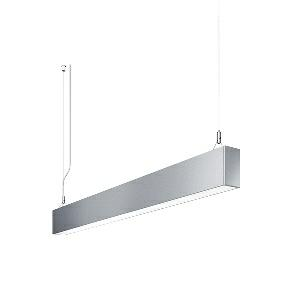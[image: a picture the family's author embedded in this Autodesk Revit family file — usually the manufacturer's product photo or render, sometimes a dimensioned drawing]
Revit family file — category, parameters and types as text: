
# Revit family: idoo_line_-_ilp_4000_vtl_d_00806468_3267
name_source: partatom
category: Lighting Fixtures
units: mm (PartAtom-declared; Revit-internal decimal feet)

## family parameters
Cut with Voids When Loaded = No
Host = Face
Light Source = No
Part Type = Normal
Room Calculation Point = No
Round Connector Dimension = Use Diameter
Shared = No

## types (1)
- IDOO.line - ILP 4000/VTL/D (1 x LED, 3850 lm, 2700-6500K)
    Apparent Load = 39 VA
    Approval mark = CE
    CIE Flux Codes = 66 91 98 40 100
    Color Rendering = 90-100
    Color Temperature = 2700-6500K
    Control Gear = Electronic ballast
    Default Elevation = 1800 mm
    Description = ILP 4000/VTL/D|Suspended luminaire|light source: LED|connected load: 220-240 V, 50/60 Hz|Power consumption: approx. 39 W|standby: approx. 0,25|luminous flux: 3850 lm|luminous efficacy: 98 lm/W|light distribution: Direct/indirect|direct ratio: approx. 40 %|colour temperature: Cold white, ca. 2700-6500 K|color rendering index (CRI): >= 90|chromaticity tolerance:  3 SDCM|System of protection: IP 40|technology: Continuously dimmable|luminaire body|material: Sectional aluminium|colour: Silver|lamp cover: Acrylic (PMMA), Clear|mains lead: 2.00 m With free stranded wires|Fastening: Steel cable 0.3 - 0.7 m|glare control: Prism aperture|luminance(L65): <= 2700 cd/m|unified glare rating(4H 8H): <=  16|special features: Specified values at approx. 4000 K, DALI Load 1x, External control required for Dali Device type 8, Flicker-free, Constant luminous flux between 2700 and 6500 K, Constant colour temperature over the whole dimming range, Suitable as emergency lighting|
    Frequency = 50 Hz
    Height = 110 mm
    Lamp = 1 x LED
    Lamp Light Flux = 3850 lm
    Lamp count = 1
    Length = 1414 mm
    Luminous efficacy = 99 lm/W
    Manufacturer = Waldmann
    ModVariant = No
    Model = 00806468
    Mounting Place = Ceiling
    Mounting Type = Pendant
    Number of Poles = 1
    OnlyDefault = Yes
    Power Factor = 1
    Product Name = IDOO.line - ILP 4000/VTL/D
    Product group = Suspended luminaire
    ProductGroupID = 9
    Protection Class = Protection class I
    Protection Degree = IP 40
    RLX_Detail_Level = 1
    RLX_Emergency_Light_Flux = 0 lm
    RLX_Emergency_Type = 0
    RLX_Emergency_Type_DB = No
    RlxData = <blob elided: 21961 chars, md5=79ec61c8>
    Socket = socket
    Standby Power = 0 W
    System Light Flux = 3850 lm
    System Power = 39 W
    Type Comments = Product without accessories
    Type Image = 113292000-00692525.jpg
    URL = http://relux.com
    VarID = ---
    Voltage = 230 V
    Voltage Range = 220-240 V
    Weight = 0.00 kg
    Width = 60 mm  [stored 0.19685 ft]

note: [stored X ft] marks values corroborated as IEEE doubles in the binary element streams (Revit-internal decimal feet)

## geometry (parser evidence)
native form markers: Blend x4, Sweep x13
no freeform markers — native parametric forms only
